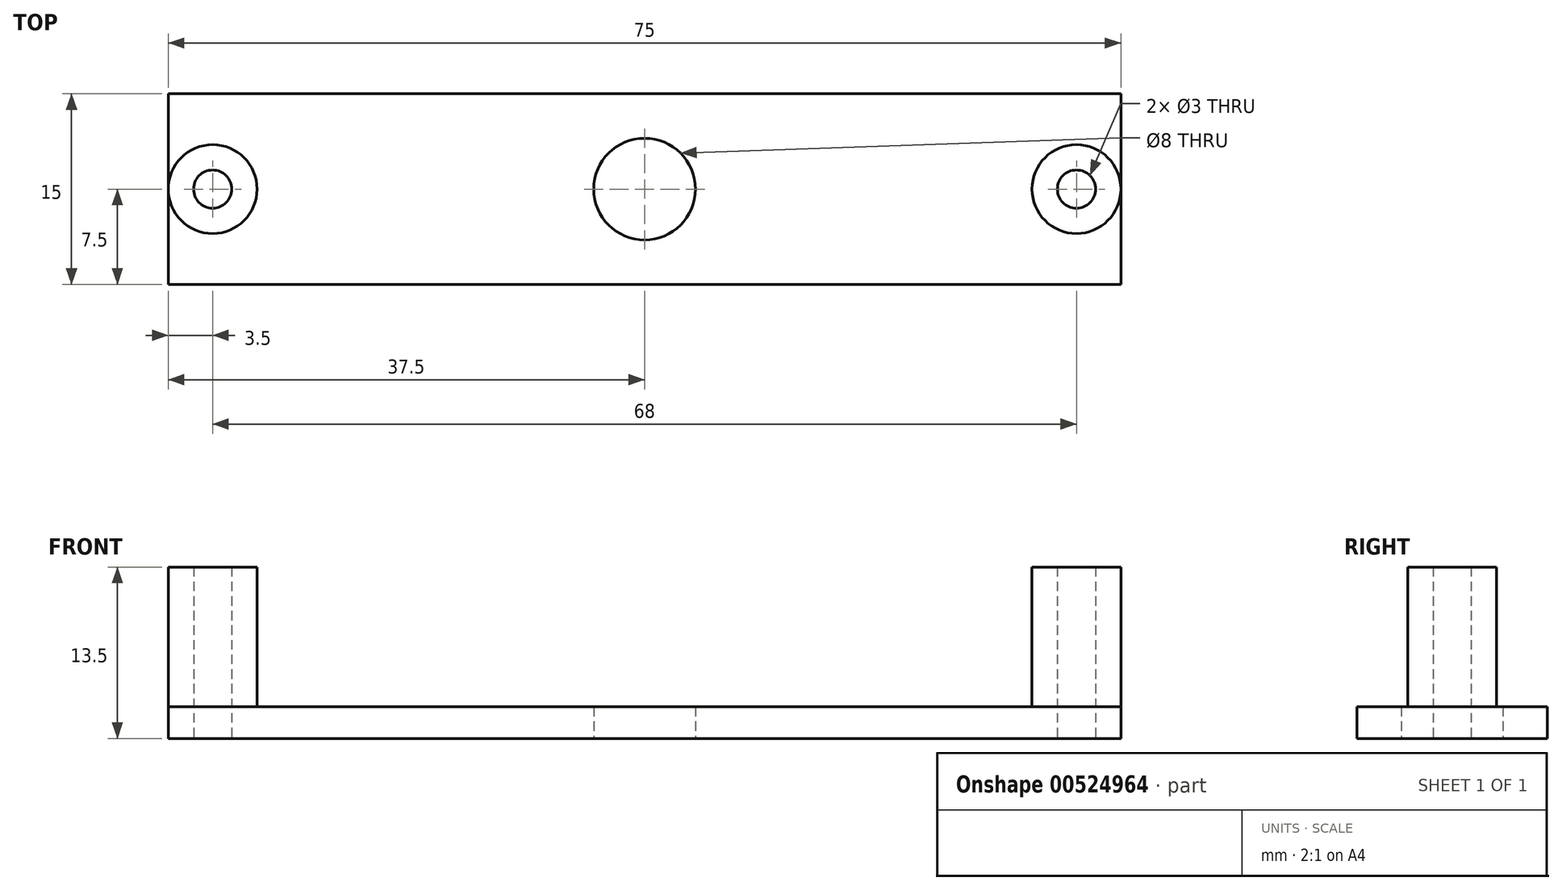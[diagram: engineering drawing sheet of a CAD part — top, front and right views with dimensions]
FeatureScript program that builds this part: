
annotation { "Feature Type Name" : "Feature", "Feature Type Description" : "" }
export const myFeature = defineFeature(function(context is Context, id is Id, definition is map)
    precondition{}
    {
        {
            var Q0;
            Q0=qCreatedBy(makeId("Top.planeOp"),FACE);
            var sketch = newSketch(context, id + "F0", { "sketchPlane" : qUnion([Q0])});
            skLineSegment(sketch, "E0.bottom", {"start": v(37.5, -7.5) * mm, "end": v(-37.5, -7.5) * mm});
            skLineSegment(sketch, "E0.top", {"start": v(37.5, 7.5) * mm, "end": v(-37.5, 7.5) * mm});
            skLineSegment(sketch, "E0.left", {"start": v(37.5, -7.5) * mm, "end": v(37.5, 7.5) * mm});
            skLineSegment(sketch, "E0.right", {"start": v(-37.5, -7.5) * mm, "end": v(-37.5, 7.5) * mm});
            skPoint(sketch, "E0.middle", {"position": v(0, 0) * mm});
            skCircle(sketch, "E1", {"center": v(-34, 0) * mm, "radius": 1.5 * mm});
            skCircle(sketch, "E2", {"center": v(34, 0) * mm, "radius": 1.5 * mm});
            skCircle(sketch, "E3", {"center": v(-34, 0) * mm, "radius": 3.5 * mm});
            skCircle(sketch, "E4", {"center": v(34, 0) * mm, "radius": 3.5 * mm});
            skLineSegment(sketch, "E5", {"start": v(-34, 0) * mm, "end": v(0, 0) * mm});
            skLineSegment(sketch, "E6", {"start": v(0, 0) * mm, "end": v(34, 0) * mm});
            skSolve(sketch);
        }
        {
            var Q0;
            Q0=makeQuery(id+"F0.imprint","IMPRINT",FACE,{"disambiguationData":[TD([[makeQuery(id+"F0.imprint","IMPRINT",EDGE,{"derivedFrom":sQuery(id+"F0.wireOp",EDGE,"E2")}),-1.0]])]});
            var Q1;
            Q1=makeQuery(id+"F0.imprint","IMPRINT",FACE,{"disambiguationData":[TD([[makeQuery(id+"F0.imprint","IMPRINT",EDGE,{"derivedFrom":sQuery(id+"F0.wireOp",EDGE,"E1")}),-1.0]])]});
            extrude(context, id + "F1", {"entities" : qUnion([Q0, Q1]), "depth" : 13.5 * mm, "offsetDistance" : 25 * mm});
        }
        {
            var Q0;
            {var subQ1=sQuery(id+"F0.wireOp",EDGE,"E0.top");Q0=makeQuery(id+"F0.imprint","IMPRINT",FACE,{"disambiguationData":[TD([[makeQuery(id+"F0.imprint","IMPRINT",EDGE,{"derivedFrom":subQ1}),1.0]])]});}
            extrude(context, id + "F2", {"entities" : qUnion([Q0]), "operationType" : NewBodyOperationType.ADD, "depth" : 2.5 * mm, "offsetDistance" : 25 * mm});
        }
        {
            var Q0;
            {var subQ5=sQuery(id+"F0.wireOp",EDGE,"E0.bottom");Q0=makeQuery(id+"F0.imprint","IMPRINT",FACE,{"disambiguationData":[TD([[makeQuery(id+"F0.imprint","IMPRINT",EDGE,{"derivedFrom":subQ5}),-1.0]])]});}
            extrude(context, id + "F3", {"entities" : qUnion([Q0]), "operationType" : NewBodyOperationType.ADD, "depth" : 2.5 * mm, "offsetDistance" : 25 * mm});
        }
        {
            var Q0;
            Q0=qCreatedBy(makeId("Top.planeOp"),FACE);
            var sketch = newSketch(context, id + "F4", { "sketchPlane" : qUnion([Q0])});
            skCircle(sketch, "E7", {"center": v(0, 0) * mm, "radius": 4 * mm});
            skSolve(sketch);
        }
        {
            var Q0;
            Q0 = qSketchRegion(id + "F4", true);
            extrude(context, id + "F5", {"entities" : qUnion([Q0]), "operationType" : NewBodyOperationType.REMOVE, "depth" : 25 * mm, "offsetDistance" : 25 * mm});
        }
    });
